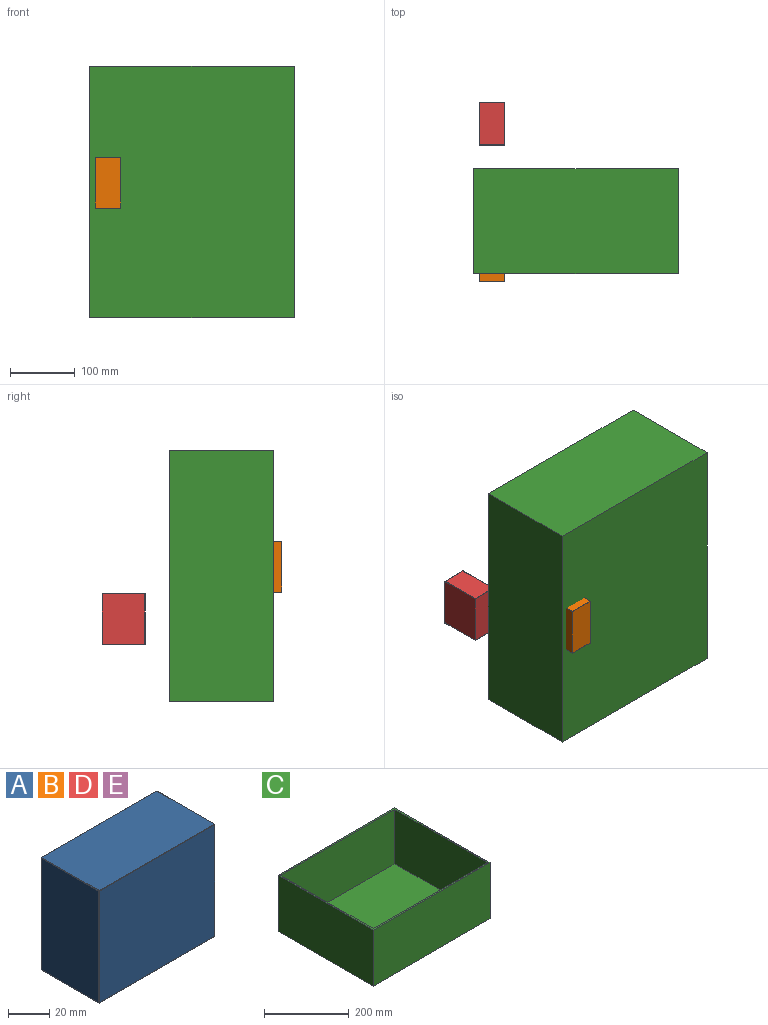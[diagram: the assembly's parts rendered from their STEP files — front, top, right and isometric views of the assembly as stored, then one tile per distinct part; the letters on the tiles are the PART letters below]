
ASSEMBLY  parts=5 mates=6
PART A: 26 faces, bbox 79.4x39.7x66.7 mm
  f0: plane 78.87x39.18mm, normal (0,0,1), area 3090mm2, adj f14,f19,f22,f25
  f1: plane 66.17x39.18mm, normal (-1,0,0), area 2592.4mm2, adj f11,f20,f21,f25
  f2: plane 78.87x39.18mm, normal (0,0,-1), area 3090mm2, adj f6,f10,f11,f12
  f3: plane 66.17x39.18mm, normal (1,0,0), area 2592.4mm2, adj f6,f9,f13,f14
  f4: plane 78.87x66.17mm, normal (0,-1,0), area 5218.4mm2, adj f9,f10,f19,f20
  f5: plane 78.87x66.17mm, normal (0,1,0), area 5218.4mm2, adj f12,f13,f21,f22
  f6: cylinder r=0.25mm len=39.18mm, axis (0,1,0), area 15.6mm2, adj f2,f3,f7,f8
  f7: sphere r=0.25mm, area 0.1mm2, adj f6,f9,f10
  f8: sphere r=0.25mm, area 0.1mm2, adj f6,f12,f13
  f9: cylinder r=0.25mm len=66.17mm, axis (0,0,-1), area 26.4mm2, adj f3,f4,f7,f15
  f10: cylinder r=0.25mm len=78.87mm, axis (-1,0,0), area 31.5mm2, adj f2,f4,f7,f16
  f11: cylinder r=0.25mm len=39.18mm, axis (0,1,0), area 15.6mm2, adj f1,f2,f16,f17
  f12: cylinder r=0.25mm len=78.87mm, axis (1,0,0), area 31.5mm2, adj f2,f5,f8,f17
  f13: cylinder r=0.25mm len=66.17mm, axis (0,0,1), area 26.4mm2, adj f3,f5,f8,f18
  f14: cylinder r=0.25mm len=39.18mm, axis (0,1,0), area 15.6mm2, adj f0,f3,f15,f18
  f15: sphere r=0.25mm, area 0.1mm2, adj f9,f14,f19
  f16: sphere r=0.25mm, area 0.1mm2, adj f10,f11,f20
  f17: sphere r=0.25mm, area 0.1mm2, adj f11,f12,f21
  f18: sphere r=0.25mm, area 0.1mm2, adj f13,f14,f22
  f19: cylinder r=0.25mm len=78.87mm, axis (1,0,0), area 31.5mm2, adj f0,f4,f15,f23
  f20: cylinder r=0.25mm len=66.17mm, axis (0,0,1), area 26.4mm2, adj f1,f4,f16,f23
  f21: cylinder r=0.25mm len=66.17mm, axis (0,0,-1), area 26.4mm2, adj f1,f5,f17,f24
  f22: cylinder r=0.25mm len=78.87mm, axis (-1,0,0), area 31.5mm2, adj f0,f5,f18,f24
  f23: sphere r=0.25mm, area 0.1mm2, adj f19,f20,f25
  f24: sphere r=0.25mm, area 0.1mm2, adj f21,f22,f25
  f25: cylinder r=0.25mm len=39.18mm, axis (0,1,0), area 15.6mm2, adj f0,f1,f23,f24
PART B: same geometry as A
PART C: 11 faces, bbox 390.7x317.5x162.1 mm
  f0: plane 390.65x317.5mm, normal (0,0,1), area 6654.4mm2, adj f1,f2,f3,f4,f6,f7,f8,f9
  f1: plane 390.65x162.05mm, normal (0,1,0), area 63305.9mm2, adj f0,f2,f4,f5
  f2: plane 317.5x162.05mm, normal (-1,0,0), area 51451.5mm2, adj f0,f1,f3,f5
  f3: plane 390.65x162.05mm, normal (0,-1,0), area 63305.9mm2, adj f0,f2,f4,f5
  f4: plane 317.5x162.05mm, normal (1,0,0), area 51451.5mm2, adj f0,f1,f3,f5
  f5: plane 390.65x317.5mm, normal (0,0,-1), area 124032mm2, adj f1,f2,f3,f4
  f6: plane 381.13x157.29mm, normal (0,-1,0), area 59947.3mm2, adj f0,f7,f9,f10
  f7: plane 307.98x157.29mm, normal (1,0,0), area 48441.2mm2, adj f0,f6,f8,f10
  f8: plane 381.13x157.29mm, normal (0,1,0), area 59947.3mm2, adj f0,f7,f9,f10
  f9: plane 307.98x157.29mm, normal (-1,0,0), area 48441.2mm2, adj f0,f6,f8,f10
  f10: plane 381.13x307.98mm, normal (0,0,1), area 117377.6mm2, adj f6,f7,f8,f9
PART D: same geometry as A
PART E: same geometry as A
PLACE A rot(axis=(-0.58,0.58,0.58),120deg) t=(-146.34,-385.64,38.6)mm
PLACE B rot(axis=(-0.58,-0.58,-0.58),120deg) t=(-104.94,-444.86,200.85)mm
PLACE C rot(axis=(-0.58,0.58,0.58),120deg) t=(5.2,-465.39,186.39)mm
PLACE D rot(axis=(-0.58,0.58,0.58),120deg) t=(-145.17,-232.88,119.51)mm
PLACE E rot(axis=(-0.58,-0.58,-0.58),120deg) t=(-0.18,-396.67,282.58)mm
MATE parallel A.f2 <-> B.f0  axis (0,-1,0) through (-126.5,-418.97,38.6)mm
MATE parallel D.f2 <-> E.f0  axis (0,-1,0) through (-125.33,-266.22,119.51)mm
MATE parallel E.f2 <-> C.f10  axis (0,-1,0) through (-20.03,-430.01,282.58)mm
MATE parallel B.f2 <-> C.f10  axis (0,-1,0) through (-124.78,-478.2,200.85)mm
MATE parallel A.f2 <-> B.f0  axis (0,-1,0) through (-126.5,-418.97,38.6)mm
MATE parallel E.f2 <-> C.f10  axis (0,-1,0) through (-20.03,-430.01,282.58)mm
